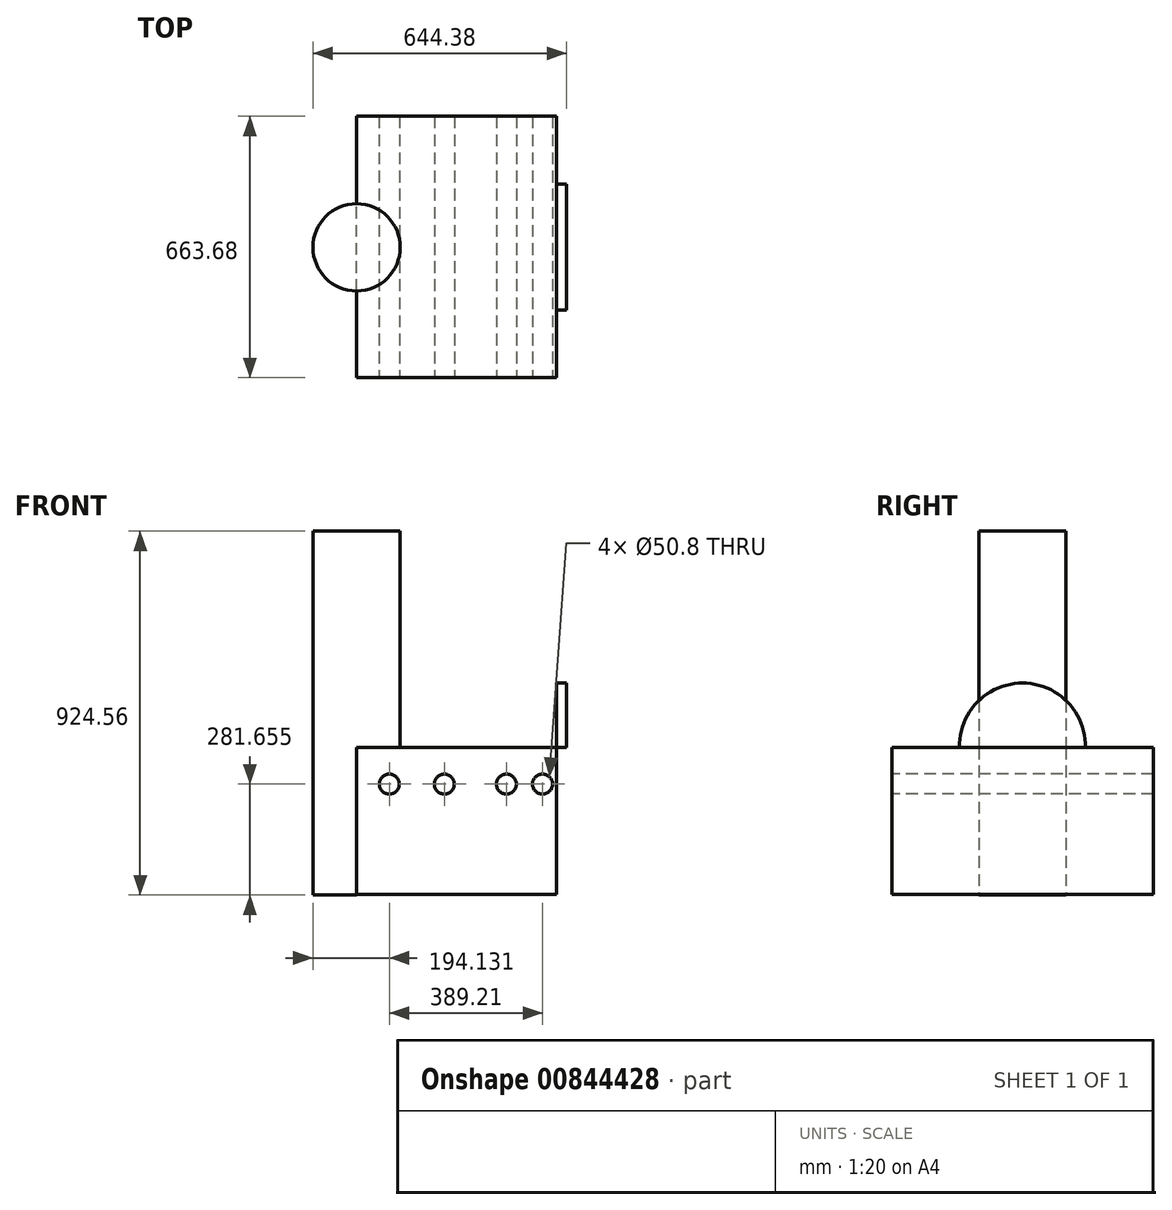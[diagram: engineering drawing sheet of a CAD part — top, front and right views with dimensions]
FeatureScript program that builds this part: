
annotation { "Feature Type Name" : "Feature", "Feature Type Description" : "" }
export const myFeature = defineFeature(function(context is Context, id is Id, definition is map)
    precondition{}
    {
        {
            var Q0;
            Q0=qCreatedBy(makeId("Top.planeOp"),FACE);
            var sketch = newSketch(context, id + "F0", { "sketchPlane" : qUnion([Q0])});
            skCircle(sketch, "E0", {"center": v(0, 0) * mm, "radius": 110.98 * mm});
            skSolve(sketch);
        }
        {
            var Q0;
            Q0=makeQuery(id+"F0.imprint","IMPRINT",FACE,{"disambiguationData":[TD([[makeQuery(id+"F0.imprint","IMPRINT",EDGE,{"derivedFrom":sQuery(id+"F0.wireOp",EDGE,"E0")}),1.0]])]});
            extrude(context, id + "F1", {"entities" : qUnion([Q0]), "depth" : 736.6 * mm, "offsetDistance" : 25.4 * mm});
        }
        {
            var Q0;
            Q0=qCreatedBy(makeId("Right.planeOp"),FACE);
            var sketch = newSketch(context, id + "F2", { "sketchPlane" : qUnion([Q0])});
            skLineSegment(sketch, "E1.bottom", {"start": v(-330.92, 186.71) * mm, "end": v(332.76, 186.71) * mm});
            skLineSegment(sketch, "E1.top", {"start": v(-330.92, -186.92) * mm, "end": v(332.76, -186.92) * mm});
            skLineSegment(sketch, "E1.left", {"start": v(-330.92, 186.71) * mm, "end": v(-330.92, -186.92) * mm});
            skLineSegment(sketch, "E1.right", {"start": v(332.76, 186.71) * mm, "end": v(332.76, -186.92) * mm});
            skSolve(sketch);
        }
        {
            var Q0;
            Q0=makeQuery(id+"F2.imprint","IMPRINT",FACE,{"disambiguationData":[TD([[makeQuery(id+"F2.imprint","IMPRINT",EDGE,{"derivedFrom":sQuery(id+"F2.wireOp",EDGE,"E1.bottom")}),-1.0]])]});
            extrude(context, id + "F3", {"entities" : qUnion([Q0]), "operationType" : NewBodyOperationType.ADD, "depth" : 508 * mm, "offsetDistance" : 25.4 * mm});
        }
        {
            var Q0;
            Q0=makeQuery(id+"F3.opExtrude","CAP_FACE",FACE,{"disambiguationData":[OSD([sQuery(id+"F2.wireOp",EDGE,"E1.bottom"),sQuery(id+"F2.wireOp",EDGE,"E1.top"),sQuery(id+"F2.wireOp",EDGE,"E1.left"),sQuery(id+"F2.wireOp",EDGE,"E1.right")])],"isStart":false});
            var sketch = newSketch(context, id + "F4", { "sketchPlane" : qUnion([Q0])});
            skArc(sketch, "E2", {"start": v(160.12, 186.71) * mm, "mid": v(0.36, 350.41) * mm, "end": v(-159.4, 186.71) * mm});
            skSolve(sketch);
        }
        {
            var Q0;
            {var subQ0=sQuery(id+"F4.wireOp",EDGE,"E2");Q0=makeQuery(id+"F4.imprint","IMPRINT",FACE,{"disambiguationData":[TD([[makeQuery(id+"F4.imprint","IMPRINT",EDGE,{"derivedFrom":subQ0}),1.0]])]});}
            extrude(context, id + "F5", {"entities" : qUnion([Q0]), "depth" : 25.4 * mm, "offsetDistance" : 25.4 * mm});
        }
        {
            var Q0;
            Q0=makeQuery(id+"F1.opExtrude","CAP_FACE",FACE,{"disambiguationData":[OSD([sQuery(id+"F0.wireOp",EDGE,"E0")])],"isStart":true});
            var sketch = newSketch(context, id + "F6", { "sketchPlane" : qUnion([Q0])});
            skArc(sketch, "E3", {"start": v(0, 110.98) * mm, "mid": v(-111.3, 0) * mm, "end": v(0, -110.98) * mm});
            skSolve(sketch);
        }
        {
            var Q0;
            {var subQ0=sQuery(id+"F0.wireOp",EDGE,"E0");Q0=makeQuery(id+"F6.imprint","IMPRINT",FACE,{"disambiguationData":[TD([[makeQuery(id+"F6.imprint","IMPRINT",EDGE,{"derivedFrom":makeQuery(id+"F1.opExtrude","CAP_EDGE",EDGE,{"disambiguationData":[OSD([subQ0])],"isStart":true})}),-1.0]])]});}
            extrude(context, id + "F7", {"entities" : qUnion([Q0]), "operationType" : NewBodyOperationType.ADD, "depth" : 25.4 * mm, "offsetDistance" : 25.4 * mm});
        }
        {
            var Q0;
            Q0=makeQuery(id+"F7.opExtrude","CAP_FACE",FACE,{"disambiguationData":[OSD([sQuery(id+"F0.wireOp",EDGE,"E0"),sQuery(id+"F2.wireOp",EDGE,"E1.bottom"),sQuery(id+"F2.wireOp",EDGE,"E1.top"),sQuery(id+"F2.wireOp",EDGE,"E1.left"),sQuery(id+"F2.wireOp",EDGE,"E1.right")])],"isStart":false});
            var sketch = newSketch(context, id + "F8", { "sketchPlane" : qUnion([Q0])});
            skArc(sketch, "E4", {"start": v(0, 110.98) * mm, "mid": v(-111.1, 0) * mm, "end": v(0, -110.98) * mm});
            skSolve(sketch);
        }
        {
            var Q0;
            {var subQ0=sQuery(id+"F0.wireOp",EDGE,"E0");Q0=makeQuery(id+"F8.imprint","IMPRINT",FACE,{"disambiguationData":[TD([[makeQuery(id+"F8.imprint","IMPRINT",EDGE,{"derivedFrom":makeQuery(id+"F7.opExtrude","CAP_EDGE",EDGE,{"disambiguationData":[OSD([subQ0])],"isStart":false})}),-1.0]])]});}
            extrude(context, id + "F9", {"entities" : qUnion([Q0]), "operationType" : NewBodyOperationType.ADD, "depth" : 162.56 * mm, "offsetDistance" : 25.4 * mm});
        }
        {
            var Q0;
            Q0=makeQuery(id+"F3.opExtrude","SWEPT_FACE",FACE,{"disambiguationData":[OSD([sQuery(id+"F2.wireOp",EDGE,"E1.left")])]});
            var sketch = newSketch(context, id + "F10", { "sketchPlane" : qUnion([Q0])});
            skPoint(sketch, "E5", {"position": v(222.95, 93.7) * mm});
            skPoint(sketch, "E6", {"position": v(83.15, 93.7) * mm});
            skPoint(sketch, "E7", {"position": v(380.65, 93.7) * mm});
            skPoint(sketch, "E8", {"position": v(472.36, 93.7) * mm});
            skSolve(sketch);
        }
        {
            var Q0;
            Q0=sQuery(id+"F10.wireOp",VERTEX,"E6");
            var Q1;
            Q1=sQuery(id+"F10.wireOp",VERTEX,"E5");
            var Q2;
            Q2=sQuery(id+"F10.wireOp",VERTEX,"E7");
            var Q3;
            Q3=sQuery(id+"F10.wireOp",VERTEX,"E8");
            var Q4;
            Q4=makeQuery(id+"F1.opExtrude","SWEPT_BODY",BODY,{"disambiguationData":[OSD([sQuery(id+"F0.wireOp",EDGE,"E0")])]});
            hole(context, id + "F11", {"style" : HoleStyle.SIMPLE, "endStyle" : HoleEndStyle.THROUGH, "holeDiameter" : 50.8 * mm, "majorDiameter" : 6.35 * mm, "isTappedThrough" : true, "tappedDepth" : 12.7 * mm, "tapClearance" : 3, "locations" : qUnion([Q0, Q1, Q2, Q3]), "scope" : qUnion([Q4])});
        }
    });
